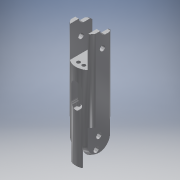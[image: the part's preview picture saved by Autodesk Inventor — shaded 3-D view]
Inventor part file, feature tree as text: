
AUTODESK INVENTOR PART (.ipt)
format: ipt  version: 2019 (Build 230136000, 136)  size: 228,864 bytes
history: imported  units: in
note: dims shown in document units (in); Inventor stores cm internally (conversion verified against a paired STEP export)
features: imported_body x1
ambient origin geometry x8: Origin, YZ Plane, XZ Plane, XY Plane, X Axis, Y Axis, Z Axis, Center Point
bodies: Solid1 (imported_parasolid)
feature tree (1):
  imported_body  NMx_Import_Brep_tag  [imported B-rep: ~12 faces, bbox_mm=[0.0, 8.0, 11.416198]]
